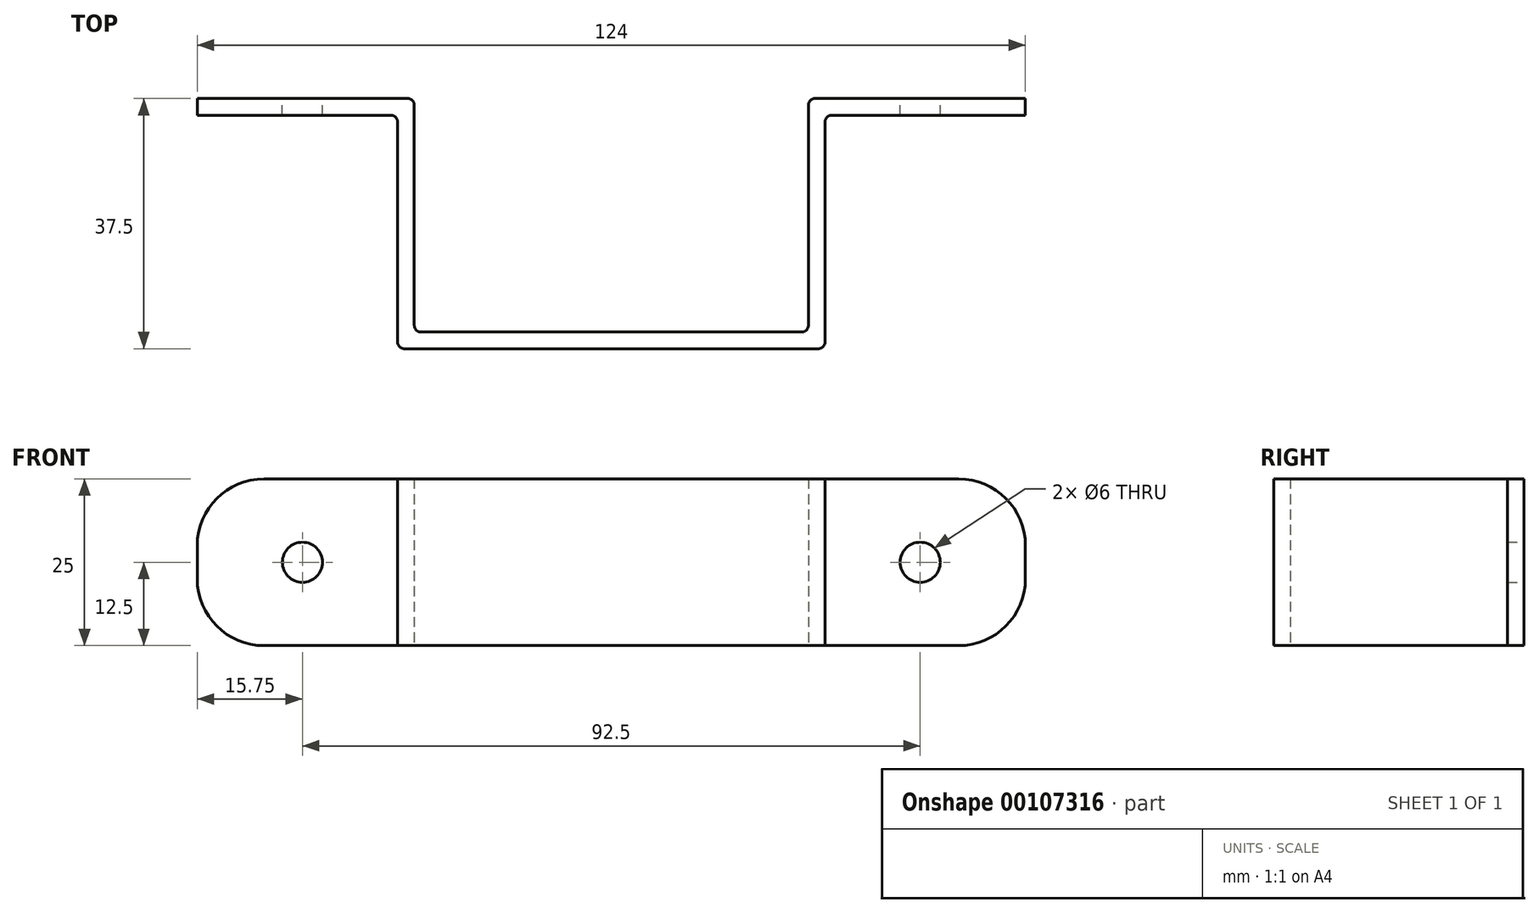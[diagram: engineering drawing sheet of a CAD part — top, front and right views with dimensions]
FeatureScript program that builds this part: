
annotation { "Feature Type Name" : "Feature", "Feature Type Description" : "" }
export const myFeature = defineFeature(function(context is Context, id is Id, definition is map)
    precondition{}
    {
        {
            var Q0;
            Q0=qCreatedBy(makeId("Top.planeOp"),FACE);
            var sketch = newSketch(context, id + "F0", { "sketchPlane" : qUnion([Q0])});
            skLineSegment(sketch, "E0", {"start": v(-30, 35) * mm, "end": v(0, 35) * mm});
            skLineSegment(sketch, "E1", {"start": v(0, 35) * mm, "end": v(0, 0) * mm});
            skLineSegment(sketch, "E2", {"start": v(0, 0) * mm, "end": v(64, 0) * mm});
            skLineSegment(sketch, "E3", {"start": v(64, 0) * mm, "end": v(64, 35) * mm});
            skLineSegment(sketch, "E4", {"start": v(64, 35) * mm, "end": v(94, 35) * mm});
            skLineSegment(sketch, "E5", {"start": v(94, 35) * mm, "end": v(94, 37.5) * mm});
            skLineSegment(sketch, "E6", {"start": v(94, 37.5) * mm, "end": v(61.5, 37.5) * mm});
            skLineSegment(sketch, "E7", {"start": v(61.5, 37.5) * mm, "end": v(61.5, 2.5) * mm});
            skLineSegment(sketch, "E8", {"start": v(61.5, 2.5) * mm, "end": v(2.5, 2.5) * mm});
            skLineSegment(sketch, "E9", {"start": v(2.5, 2.5) * mm, "end": v(2.5, 37.5) * mm});
            skLineSegment(sketch, "E10", {"start": v(2.5, 37.5) * mm, "end": v(-30, 37.5) * mm});
            skLineSegment(sketch, "E11", {"start": v(-30, 37.5) * mm, "end": v(-30, 35) * mm});
            skSolve(sketch);
        }
        {
            var Q0;
            Q0=makeQuery(id+"F0.imprint","IMPRINT",FACE,{"disambiguationData":[TD([[makeQuery(id+"F0.imprint","IMPRINT",EDGE,{"derivedFrom":sQuery(id+"F0.wireOp",EDGE,"E0")}),1.0]])]});
            extrude(context, id + "F1", {"entities" : qUnion([Q0]), "depth" : 25 * mm});
        }
        {
            var Q0;
            Q0=makeQuery(id+"F1.opExtrude","CAP_EDGE",EDGE,{"disambiguationData":[OSD([sQuery(id+"F0.wireOp",EDGE,"E11")])],"isStart":false});
            var Q1;
            Q1=makeQuery(id+"F1.opExtrude","CAP_EDGE",EDGE,{"disambiguationData":[OSD([sQuery(id+"F0.wireOp",EDGE,"E11")])],"isStart":true});
            var Q2;
            Q2=makeQuery(id+"F1.opExtrude","CAP_EDGE",EDGE,{"disambiguationData":[OSD([sQuery(id+"F0.wireOp",EDGE,"E5")])],"isStart":true});
            var Q3;
            Q3=makeQuery(id+"F1.opExtrude","CAP_EDGE",EDGE,{"disambiguationData":[OSD([sQuery(id+"F0.wireOp",EDGE,"E5")])],"isStart":false});
            fillet(context, id + "F2", {"entities" : qUnion([Q0, Q1, Q2, Q3]), "radius" : 10 * mm, "tangentPropagation" : true, "allowEdgeOverflow" : false});
        }
        {
            var Q0;
            Q0=makeQuery(id+"F1.opExtrude","SWEPT_EDGE",EDGE,{"disambiguationData":[OSD([sQuery(id+"F0.wireOp",EDGE,"E3"),sQuery(id+"F0.wireOp",EDGE,"E4")])]});
            var Q1;
            Q1=makeQuery(id+"F1.opExtrude","SWEPT_EDGE",EDGE,{"disambiguationData":[OSD([sQuery(id+"F0.wireOp",EDGE,"E2"),sQuery(id+"F0.wireOp",EDGE,"E3")])]});
            var Q2;
            Q2=makeQuery(id+"F1.opExtrude","SWEPT_EDGE",EDGE,{"disambiguationData":[OSD([sQuery(id+"F0.wireOp",EDGE,"E1"),sQuery(id+"F0.wireOp",EDGE,"E2")])]});
            var Q3;
            Q3=makeQuery(id+"F1.opExtrude","SWEPT_EDGE",EDGE,{"disambiguationData":[OSD([sQuery(id+"F0.wireOp",EDGE,"E0"),sQuery(id+"F0.wireOp",EDGE,"E1")])]});
            var Q4;
            Q4=makeQuery(id+"F1.opExtrude","SWEPT_EDGE",EDGE,{"disambiguationData":[OSD([sQuery(id+"F0.wireOp",EDGE,"E9"),sQuery(id+"F0.wireOp",EDGE,"E10")])]});
            var Q5;
            Q5=makeQuery(id+"F1.opExtrude","SWEPT_EDGE",EDGE,{"disambiguationData":[OSD([sQuery(id+"F0.wireOp",EDGE,"E8"),sQuery(id+"F0.wireOp",EDGE,"E9")])]});
            var Q6;
            Q6=makeQuery(id+"F1.opExtrude","SWEPT_EDGE",EDGE,{"disambiguationData":[OSD([sQuery(id+"F0.wireOp",EDGE,"E7"),sQuery(id+"F0.wireOp",EDGE,"E8")])]});
            var Q7;
            Q7=makeQuery(id+"F1.opExtrude","SWEPT_EDGE",EDGE,{"disambiguationData":[OSD([sQuery(id+"F0.wireOp",EDGE,"E6"),sQuery(id+"F0.wireOp",EDGE,"E7")])]});
            fillet(context, id + "F3", {"entities" : qUnion([Q0, Q1, Q2, Q3, Q4, Q5, Q6, Q7]), "radius" : 1 * mm, "tangentPropagation" : true, "allowEdgeOverflow" : false});
        }
        {
            var Q0;
            Q0=makeQuery(id+"F1.opExtrude","SWEPT_FACE",FACE,{"disambiguationData":[OSD([sQuery(id+"F0.wireOp",EDGE,"E10")])]});
            var sketch = newSketch(context, id + "F4", { "sketchPlane" : qUnion([Q0])});
            skCircle(sketch, "E12", {"center": v(14.25, 12.5) * mm, "radius": 3 * mm});
            skPoint(sketch, "E12.centerSnap0", {"position": v(-1.5, 12.5) * mm});
            skCircle(sketch, "E13", {"center": v(-78.25, 12.5) * mm, "radius": 3 * mm});
            skLineSegment(sketch, "E14", {"start": v(30, 12.5) * mm, "end": v(-1.5, 12.5) * mm, "construction": true});
            skLineSegment(sketch, "E15", {"start": v(-62.5, 12.5) * mm, "end": v(-94, 12.5) * mm, "construction": true});
            skSolve(sketch);
        }
        {
            var Q0;
            Q0 = qSketchRegion(id + "F4", true);
            extrude(context, id + "F5", {"entities" : qUnion([Q0]), "operationType" : NewBodyOperationType.REMOVE, "oppositeDirection" : true, "depth" : 25 * mm});
        }
    });
